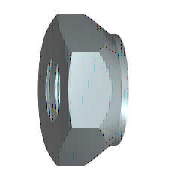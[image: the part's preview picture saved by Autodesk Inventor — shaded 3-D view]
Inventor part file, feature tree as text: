
AUTODESK INVENTOR PART (.ipt)
format: ipt  version: 2018 (Build 220112000, 112)  size: 184,832 bytes
history: native  units: mm (DEFAULTED — no unit token found)
features: sketch x3, hole x1, chamfer x1, other x1, plane x1
ambient origin geometry x7: Origin, YZ Plane, XZ Plane, X Axis, Y Axis, Z Axis, Center Point
bodies: Solid1 (feature_tree), Body (feature_tree)
feature tree (7):
  hole  "Thread"  [1 undecoded]
  chamfer  "Chamfer3"  Distance=8.0mm
  other  "Work Axis1"
  plane  "Work Plane1"
  sketch  "Sketch1"  dims[d0=9.237604mm d1=5.3mm]
  sketch  "Sketch3"  dims[d3=30.0deg d5=8.0mm d6=6.8mm d7=90.0deg d8=8.726646mm d9=2.7mm d24=4.134mm d25=6.0mm d26=4.0mm d27=2.0mm d28=14.3117mm d29=8.0mm d30=20.594885mm d10=0.433013mm d11=30.0deg d12=0.433013mm d13=30.0deg d14=0.0mm d38=0.0mm d39=0.433013mm d40=0.433013mm d41=0.0mm d42=0.0mm]
  sketch  "Sketch2"  dims[d2=0.0mm]
note: 1 required parameter value undecoded (feature->parameter linkage not recoverable at this tier; creation-order binding heuristic only, values carry confidence <= 0.55)
